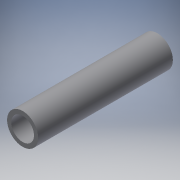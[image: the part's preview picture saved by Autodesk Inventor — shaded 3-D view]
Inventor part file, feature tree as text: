
AUTODESK INVENTOR PART (.ipt)
format: ipt  version: 2019 (Build 230136000, 136)  size: 100,864 bytes
history: native  units: mm
features: extrude x2, sketch x2
ambient origin geometry x8: Origin, YZ Plane, XZ Plane, XY Plane, X Axis, Y Axis, Z Axis, Center Point
bodies: Solid1 (feature_tree)
feature tree (4):
  extrude  "Extrusion1"  Depth=650.0mm TaperAngle=0.0deg
  extrude  "Extrusion2"  Depth=71.05mm TaperAngle=0.0deg
  sketch  "Sketch1"  dims[d0=150.0mm d1=650.0mm d2=0.0mm]
  sketch  "Sketch2"  dims[d3=110.0mm d4=71.05mm d5=0.0mm]
